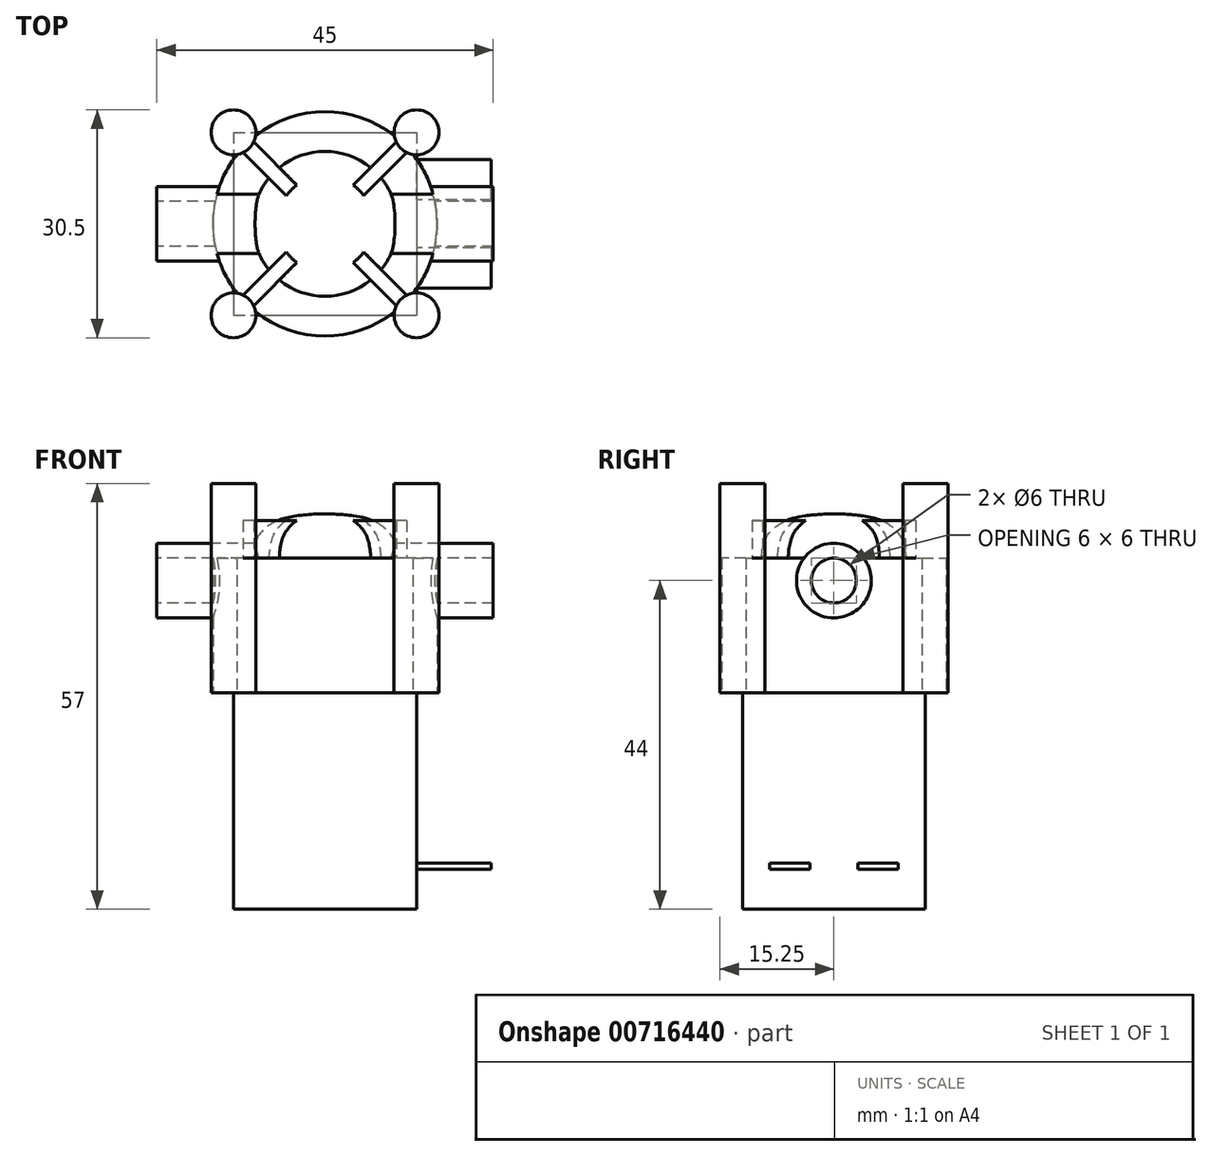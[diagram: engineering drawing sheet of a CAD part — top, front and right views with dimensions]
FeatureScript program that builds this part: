
annotation { "Feature Type Name" : "Feature", "Feature Type Description" : "" }
export const myFeature = defineFeature(function(context is Context, id is Id, definition is map)
    precondition{}
    {
        {
            var Q0;
            Q0=qCreatedBy(makeId("Top.planeOp"),FACE);
            var sketch = newSketch(context, id + "F0", { "sketchPlane" : qUnion([Q0])});
            skLineSegment(sketch, "E0", {"start": v(0, -30.4) * mm, "end": v(0, 42.81) * mm, "construction": true});
            skLineSegment(sketch, "E1", {"start": v(-43.65, 0) * mm, "end": v(49.75, 0) * mm, "construction": true});
            skCircle(sketch, "E2", {"center": v(0, 0) * mm, "radius": 15 * mm});
            skSolve(sketch);
        }
        {
            var Q0;
            Q0 = qSketchRegion(id + "F0", true);
            extrude(context, id + "F1", {"entities" : qUnion([Q0]), "flatOperationType" : FlatOperationType.REMOVE, "depth" : 18 * mm, "offsetDistance" : 25 * mm, "domain" : OperationDomain.MODEL});
        }
        {
            var Q0;
            Q0=makeQuery(id+"F1.opExtrude","CAP_FACE",FACE,{"disambiguationData":[OSD([sQuery(id+"F0.wireOp",EDGE,"E2")])],"isStart":true});
            var sketch = newSketch(context, id + "F2", { "sketchPlane" : qUnion([Q0])});
            skCircle(sketch, "E3", {"center": v(12.25, -12.25) * mm, "radius": 3 * mm});
            skCircle(sketch, "E4.MirrorC", {"center": v(-12.25, -12.25) * mm, "radius": 3 * mm});
            skCircle(sketch, "E5.MirrorC", {"center": v(-12.25, 12.25) * mm, "radius": 3 * mm});
            skCircle(sketch, "E6.MirrorC", {"center": v(12.25, 12.25) * mm, "radius": 3 * mm});
            skSolve(sketch);
        }
        {
            var Q0;
            Q0 = qSketchRegion(id + "F2", true);
            extrude(context, id + "F3", {"entities" : qUnion([Q0]), "operationType" : NewBodyOperationType.ADD, "flatOperationType" : FlatOperationType.REMOVE, "oppositeDirection" : true, "depth" : 28 * mm, "offsetDistance" : 25 * mm, "domain" : OperationDomain.MODEL});
        }
        {
            var Q0;
            Q0=makeQuery(id+"F1.opExtrude","CAP_FACE",FACE,{"disambiguationData":[OSD([sQuery(id+"F0.wireOp",EDGE,"E2")])],"isStart":false});
            var sketch = newSketch(context, id + "F4", { "sketchPlane" : qUnion([Q0])});
            skArc(sketch, "E7.0.startCap", {"start": v(12.96, -11.54) * mm, "mid": v(12.96, -12.96) * mm, "end": v(11.54, -12.96) * mm});
            skArc(sketch, "E7.0.endCap", {"start": v(-12.96, 11.54) * mm, "mid": v(-12.96, 12.96) * mm, "end": v(-11.54, 12.96) * mm});
            skLineSegment(sketch, "E7.0.left", {"start": v(11.54, -12.96) * mm, "end": v(0, -1.41) * mm});
            skLineSegment(sketch, "E7.0.right", {"start": v(12.96, -11.54) * mm, "end": v(1.41, 0) * mm});
            skArc(sketch, "E8.0.startCap", {"start": v(11.54, 12.96) * mm, "mid": v(12.96, 12.96) * mm, "end": v(12.96, 11.54) * mm});
            skArc(sketch, "E8.0.endCap", {"start": v(-11.54, -12.96) * mm, "mid": v(-12.96, -12.96) * mm, "end": v(-12.96, -11.54) * mm});
            skLineSegment(sketch, "E8.0.left", {"start": v(12.96, 11.54) * mm, "end": v(1.41, 0) * mm});
            skLineSegment(sketch, "E8.0.right", {"start": v(11.54, 12.96) * mm, "end": v(0, 1.41) * mm});
            skLineSegment(sketch, "E9.trimOffspring", {"start": v(0, 1.41) * mm, "end": v(-11.54, 12.96) * mm});
            skLineSegment(sketch, "E10.trimOffspring", {"start": v(-1.41, 0) * mm, "end": v(-12.96, 11.54) * mm});
            skLineSegment(sketch, "E11.trimOffspring", {"start": v(0, -1.41) * mm, "end": v(-11.54, -12.96) * mm});
            skLineSegment(sketch, "E12.trimOffspring", {"start": v(-1.41, 0) * mm, "end": v(-12.96, -11.54) * mm});
            skSolve(sketch);
        }
        {
            var Q0;
            Q0 = qSketchRegion(id + "F4", true);
            extrude(context, id + "F5", {"entities" : qUnion([Q0]), "operationType" : NewBodyOperationType.ADD, "depth" : 5 * mm, "offsetDistance" : 25 * mm});
        }
        {
            var Q0;
            Q0=qCreatedBy(makeId("Front.planeOp"),FACE);
            var sketch = newSketch(context, id + "F6", { "sketchPlane" : qUnion([Q0])});
            skLineSegment(sketch, "E13", {"start": v(0, 17.88) * mm, "end": v(0, 23.93) * mm});
            skLineSegment(sketch, "E14", {"start": v(0, 17.88) * mm, "end": v(-9.7, 17.88) * mm});
            skFitSpline(sketch, "E15", {"points": [v(0, 23.93) * mm, v(-0.7, 23.93) * mm, v(-3.1, 23.75) * mm, v(-5.47, 23.34) * mm, v(-7.18, 22.6) * mm, v(-8.96, 20.92) * mm, v(-9.7, 17.88) * mm], "startDerivative": vector(-5.68, 0.28) * mm, "endDerivative": vector(-0.22, -14.29) * mm});
            skSolve(sketch);
        }
        {
            var Q0;
            Q0=qCreatedBy(makeId("Front.planeOp"),FACE);
            var sketch = newSketch(context, id + "F7", { "sketchPlane" : qUnion([Q0])});
            skLineSegment(sketch, "E16", {"start": v(0, 31.61) * mm, "end": v(0, -24.43) * mm, "construction": true});
            skSolve(sketch);
        }
        {
            var Q0;
            Q0 = qSketchRegion(id + "F6", true);
            var Q1;
            Q1=sQuery(id+"F7.wireOp",EDGE,"E16");
            revolve(context, id + "F8", {"surfaceOperationType" : NewSurfaceOperationType.NEW, "entities" : qUnion([Q0]), "axis" : qUnion([Q1]), "revolveType" : RevolveType.FULL});
        }
        {
            var Q0;
            Q0=makeQuery(id+"F3.boolean.opBoolean","MERGE",FACE,{"derivedFrom":[makeQuery(id+"F1.opExtrude","CAP_FACE",FACE,{"disambiguationData":[OSD([sQuery(id+"F0.wireOp",EDGE,"E2")])],"isStart":true}),makeQuery(id+"F3.opExtrude","CAP_FACE",FACE,{"disambiguationData":[OSD([sQuery(id+"F2.wireOp",EDGE,"E3")])],"isStart":true}),makeQuery(id+"F3.opExtrude","CAP_FACE",FACE,{"disambiguationData":[OSD([sQuery(id+"F2.wireOp",EDGE,"E4.MirrorC")])],"isStart":true}),makeQuery(id+"F3.opExtrude","CAP_FACE",FACE,{"disambiguationData":[OSD([sQuery(id+"F2.wireOp",EDGE,"E5.MirrorC")])],"isStart":true}),makeQuery(id+"F3.opExtrude","CAP_FACE",FACE,{"disambiguationData":[OSD([sQuery(id+"F2.wireOp",EDGE,"E6.MirrorC")])],"isStart":true})]});
            var sketch = newSketch(context, id + "F9", { "sketchPlane" : qUnion([Q0])});
            skLineSegment(sketch, "E17.bottom", {"start": v(-12.25, -12.25) * mm, "end": v(12.25, -12.25) * mm});
            skLineSegment(sketch, "E17.top", {"start": v(-12.25, 12.25) * mm, "end": v(12.25, 12.25) * mm});
            skLineSegment(sketch, "E17.left", {"start": v(-12.25, -12.25) * mm, "end": v(-12.25, 12.25) * mm});
            skLineSegment(sketch, "E17.right", {"start": v(12.25, -12.25) * mm, "end": v(12.25, 12.25) * mm});
            skPoint(sketch, "E17.middle", {"position": v(0, 0) * mm});
            skSolve(sketch);
        }
        {
            var Q0;
            Q0 = qSketchRegion(id + "F9", true);
            extrude(context, id + "F10", {"entities" : qUnion([Q0]), "operationType" : NewBodyOperationType.ADD, "flatOperationType" : FlatOperationType.REMOVE, "depth" : 29 * mm, "offsetDistance" : 25 * mm, "domain" : OperationDomain.MODEL});
        }
        {
            var Q0;
            Q0=makeQuery(id+"F10.opExtrude","SWEPT_FACE",FACE,{"disambiguationData":[OSD([sQuery(id+"F9.wireOp",EDGE,"E17.right")])]});
            var sketch = newSketch(context, id + "F11", { "sketchPlane" : qUnion([Q0])});
            skLineSegment(sketch, "E18.bottom", {"start": v(3.2, -22.8) * mm, "end": v(8.6, -22.8) * mm});
            skLineSegment(sketch, "E18.top", {"start": v(3.2, -23.65) * mm, "end": v(8.6, -23.65) * mm});
            skLineSegment(sketch, "E18.left", {"start": v(3.2, -22.8) * mm, "end": v(3.2, -23.65) * mm});
            skLineSegment(sketch, "E18.right", {"start": v(8.6, -22.8) * mm, "end": v(8.6, -23.65) * mm});
            skPoint(sketch, "E18.middle", {"position": v(5.9, -23.22) * mm});
            skPoint(sketch, "E19.MirrorP", {"position": v(-5.9, -23.22) * mm});
            skLineSegment(sketch, "E20.MirrorCS", {"start": v(-3.2, -22.8) * mm, "end": v(-8.6, -22.8) * mm});
            skLineSegment(sketch, "E21.MirrorCS", {"start": v(-3.2, -23.65) * mm, "end": v(-8.6, -23.65) * mm});
            skLineSegment(sketch, "E22.MirrorCS", {"start": v(-8.6, -22.8) * mm, "end": v(-8.6, -23.65) * mm});
            skLineSegment(sketch, "E23.MirrorCS", {"start": v(-3.2, -22.8) * mm, "end": v(-3.2, -23.65) * mm});
            skSolve(sketch);
        }
        {
            var Q0;
            Q0 = qSketchRegion(id + "F11", true);
            extrude(context, id + "F12", {"entities" : qUnion([Q0]), "operationType" : NewBodyOperationType.ADD, "depth" : 10 * mm, "offsetDistance" : 25 * mm});
        }
        {
            var Q0;
            Q0=qCreatedBy(makeId("Right.planeOp"),FACE);
            var sketch = newSketch(context, id + "F13", { "sketchPlane" : qUnion([Q0])});
            skCircle(sketch, "E24", {"center": v(0, 15) * mm, "radius": 5 * mm});
            skCircle(sketch, "E25", {"center": v(0, 15) * mm, "radius": 3 * mm});
            skSolve(sketch);
        }
        {
            var Q0;
            Q0 = qSketchRegion(id + "F13", true);
            extrude(context, id + "F14", {"entities" : qUnion([Q0]), "operationType" : NewBodyOperationType.ADD, "depth" : 45 * mm, "offsetDistance" : 25 * mm, "symmetric" : true});
        }
    });
